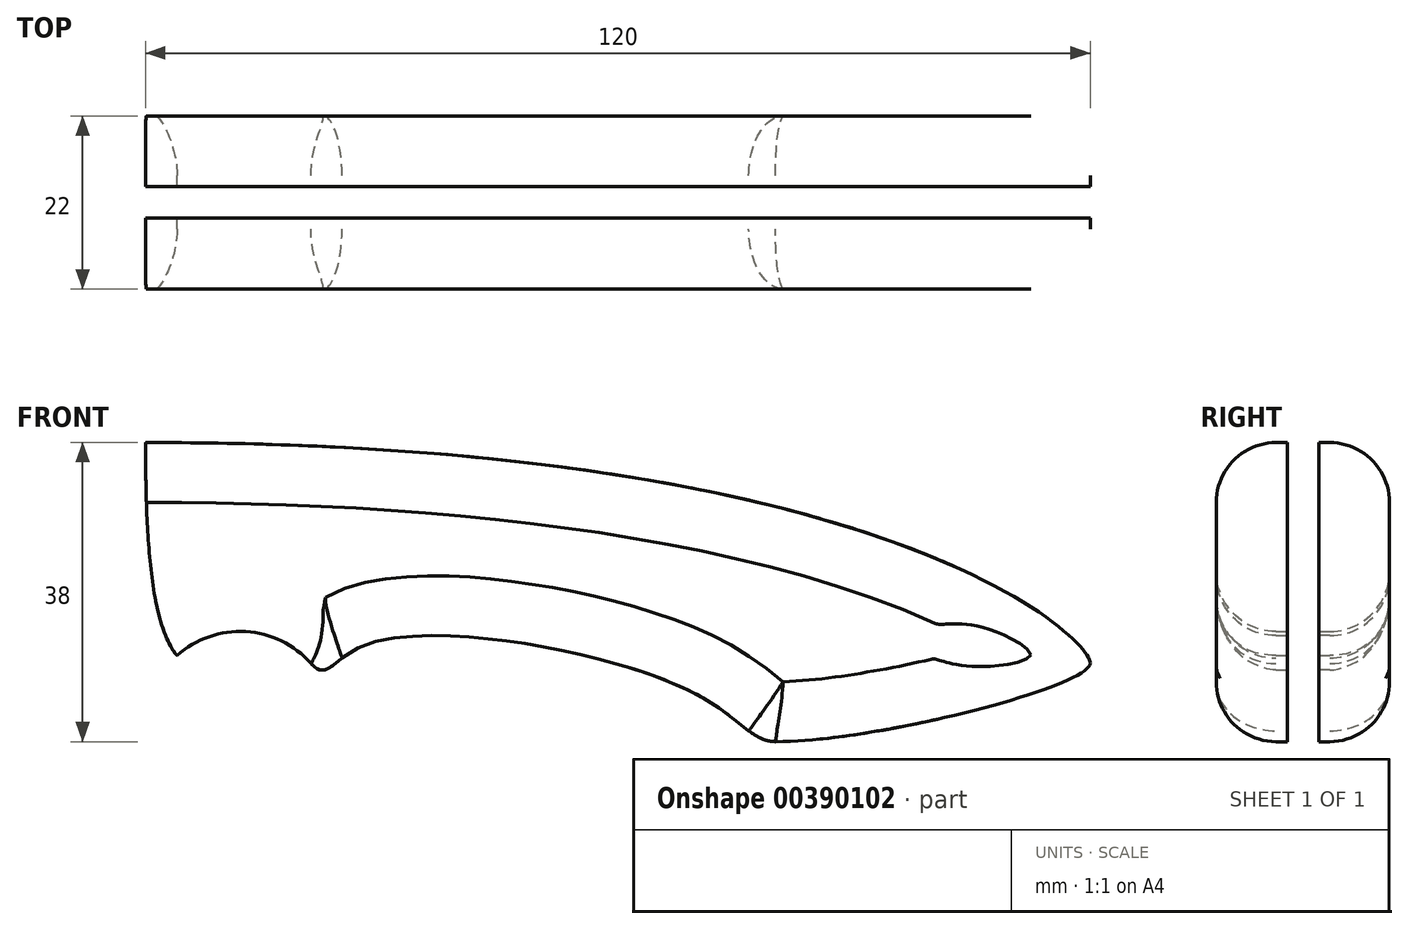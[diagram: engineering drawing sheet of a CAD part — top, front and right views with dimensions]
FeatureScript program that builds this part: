
annotation { "Feature Type Name" : "Feature", "Feature Type Description" : "" }
export const myFeature = defineFeature(function(context is Context, id is Id, definition is map)
    precondition{}
    {
        {
            var Q0;
            Q0=qCreatedBy(makeId("Front.planeOp"),FACE);
            var sketch = newSketch(context, id + "F0", { "sketchPlane" : qUnion([Q0])});
            skLineSegment(sketch, "E0.bottom", {"start": v(0, 0) * mm, "end": v(230, 0) * mm});
            skLineSegment(sketch, "E0.top", {"start": v(0, -38) * mm, "end": v(230, -38) * mm});
            skLineSegment(sketch, "E0.left", {"start": v(0, 0) * mm, "end": v(0, -38) * mm});
            skLineSegment(sketch, "E0.right", {"start": v(230, 0) * mm, "end": v(230, -38) * mm});
            skSolve(sketch);
        }
        {
            var Q0;
            Q0=makeQuery(id+"F0.imprint","IMPRINT",FACE,{"disambiguationData":[TD([[makeQuery(id+"F0.imprint","IMPRINT",EDGE,{"derivedFrom":sQuery(id+"F0.wireOp",EDGE,"E0.bottom")}),-1.0]])]});
            var sketch = newSketch(context, id + "F1", { "sketchPlane" : qUnion([Q0])});
            skLineSegment(sketch, "E1", {"start": v(0, 0) * mm, "end": v(0, -12) * mm});
            skLineSegment(sketch, "E2", {"start": v(110, 0) * mm, "end": v(230, 0) * mm});
            skFitSpline(sketch, "E3", {"points": [v(0, -12) * mm, v(110, 0) * mm], "startDerivative": vector(36.23, 12.3) * mm, "endDerivative": vector(240, 0) * mm});
            skFitSpline(sketch, "E4", {"points": [v(0, -12) * mm, v(110, -38) * mm], "startDerivative": vector(39.03, -50.57) * mm, "endDerivative": vector(165, 0) * mm});
            skFitSpline(sketch, "E5", {"points": [v(110, 0) * mm, v(230, -28) * mm], "startDerivative": vector(285, 0) * mm, "endDerivative": vector(0, -9) * mm});
            skLineSegment(sketch, "E6", {"start": v(110, -38) * mm, "end": v(110, -36) * mm});
            skLineSegment(sketch, "E7", {"start": v(110, -36) * mm, "end": v(122, -36) * mm, "construction": true});
            skArc(sketch, "E8", {"start": v(131, -28.06) * mm, "mid": v(117.76, -24.78) * mm, "end": v(110, -36) * mm});
            skLineSegment(sketch, "E9", {"start": v(131, -28.06) * mm, "end": v(132.98, -30.31) * mm});
            skFitSpline(sketch, "E10", {"points": [v(190, -38) * mm, v(180, -32) * mm, v(137, -26.06) * mm, v(131, -28.06) * mm], "startDerivative": vector(-33, 0) * mm, "endDerivative": vector(-29.63, 33.6) * mm});
            skFitSpline(sketch, "E11", {"points": [v(230, -28) * mm, v(190, -38) * mm], "startDerivative": vector(0, -9) * mm, "endDerivative": vector(-39, 0) * mm});
            skLineSegment(sketch, "E12", {"start": v(110, -28.06) * mm, "end": v(131, -28.06) * mm, "construction": true});
            skLineSegment(sketch, "E13", {"start": v(131, -26.06) * mm, "end": v(137, -26.06) * mm, "construction": true});
            skLineSegment(sketch, "E14", {"start": v(131, -28.06) * mm, "end": v(131, -26.06) * mm, "construction": true});
            skLineSegment(sketch, "E15", {"start": v(190, -38) * mm, "end": v(187, -38) * mm});
            skLineSegment(sketch, "E16", {"start": v(190, -32) * mm, "end": v(180, -32) * mm, "construction": true});
            skLineSegment(sketch, "E17", {"start": v(190, -38) * mm, "end": v(190, -32) * mm, "construction": true});
            skLineSegment(sketch, "E18", {"start": v(190, -38) * mm, "end": v(203, -38) * mm, "construction": true});
            skLineSegment(sketch, "E19", {"start": v(190, -38) * mm, "end": v(230, -38) * mm, "construction": true});
            skLineSegment(sketch, "E20", {"start": v(230, -28) * mm, "end": v(230, -25) * mm, "construction": true});
            skLineSegment(sketch, "E21", {"start": v(230, -28) * mm, "end": v(230, -31) * mm, "construction": true});
            skLineSegment(sketch, "E22", {"start": v(230, -28) * mm, "end": v(230, -38) * mm, "construction": true});
            skLineSegment(sketch, "E23", {"start": v(110, 0) * mm, "end": v(30, 0) * mm, "construction": true});
            skLineSegment(sketch, "E24", {"start": v(0, 0) * mm, "end": v(110, 0) * mm, "construction": true});
            skLineSegment(sketch, "E25", {"start": v(110, 0) * mm, "end": v(205, 0) * mm});
            skLineSegment(sketch, "E26", {"start": v(0, -12) * mm, "end": v(12.08, -7.9) * mm});
            skLineSegment(sketch, "E27", {"start": v(0, -12) * mm, "end": v(13.01, -28.86) * mm});
            skLineSegment(sketch, "E28", {"start": v(110, -27.06) * mm, "end": v(114, -27.06) * mm, "construction": true});
            skLineSegment(sketch, "E29", {"start": v(114, -27.06) * mm, "end": v(110, -22.58) * mm, "construction": true});
            skFitSpline(sketch, "E30", {"points": [v(110, 0) * mm, v(114, -27.06) * mm], "startDerivative": vector(0, -21) * mm, "endDerivative": vector(12, -13.42) * mm});
            skLineSegment(sketch, "E31", {"start": v(110, 0) * mm, "end": v(110, -7) * mm, "construction": true});
            skLineSegment(sketch, "E32", {"start": v(110, 0) * mm, "end": v(107, 0) * mm});
            skLineSegment(sketch, "E33", {"start": v(107, 0) * mm, "end": v(97, 0) * mm});
            skLineSegment(sketch, "E34", {"start": v(97, 0) * mm, "end": v(97, -14) * mm});
            skLineSegment(sketch, "E35", {"start": v(97, -14) * mm, "end": v(97, -24) * mm, "construction": true});
            skArc(sketch, "E36", {"start": v(107, -24) * mm, "mid": v(104.07, -16.92) * mm, "end": v(97, -14) * mm});
            skPoint(sketch, "E37", {"position": v(107, -24) * mm});
            skLineSegment(sketch, "E38", {"start": v(107, -24) * mm, "end": v(107, -38) * mm});
            skLineSegment(sketch, "E39", {"start": v(110, -38) * mm, "end": v(55, -38) * mm, "construction": true});
            skSolve(sketch);
        }
        {
            var Q0;
            {var subQ4=sQuery(id+"F1.wireOp",EDGE,"E3");Q0=makeQuery(id+"F1.imprint","IMPRINT",FACE,{"disambiguationData":[TD([[makeQuery(id+"F1.imprint","IMPRINT",EDGE,{"derivedFrom":subQ4}),-1.0]])]});}
            extrude(context, id + "F2", {"entities" : qUnion([Q0]), "endBound" : BoundingType.SYMMETRIC, "depth" : 4 * mm});
        }
        {
            var Q0;
            {var subQ5=sQuery(id+"F1.wireOp",EDGE,"E36");Q0=makeQuery(id+"F1.imprint","IMPRINT",FACE,{"disambiguationData":[TD([[makeQuery(id+"F1.imprint","IMPRINT",EDGE,{"derivedFrom":subQ5}),1.0]])]});}
            extrude(context, id + "F3", {"entities" : qUnion([Q0]), "operationType" : NewBodyOperationType.ADD, "endBound" : BoundingType.SYMMETRIC, "depth" : 4 * mm});
        }
        {
            var Q0;
            Q0=makeQuery(id+"F3.opExtrude","CAP_EDGE",EDGE,{"disambiguationData":[OSD([sQuery(id+"F1.wireOp",EDGE,"E4")])],"isStart":false});
            var Q1;
            Q1=makeQuery(id+"F3.opExtrude","CAP_EDGE",EDGE,{"disambiguationData":[OSD([sQuery(id+"F1.wireOp",EDGE,"E4")])],"isStart":true});
            chamfer(context, id + "F4", {"entities" : qUnion([Q0, Q1]), "chamferType" : ChamferType.TWO_OFFSETS, "width1" : 24 * mm, "oppositeDirection" : false, "width2" : 2 * mm, "tangentPropagation" : true});
        }
        {
            var Q0;
            {var subQ1=sQuery(id+"F1.wireOp",EDGE,"E6");Q0=makeQuery(id+"F1.imprint","IMPRINT",FACE,{"disambiguationData":[TD([[makeQuery(id+"F1.imprint","IMPRINT",EDGE,{"derivedFrom":subQ1}),1.0]])]});}
            var Q1;
            Q1=makeQuery(id+"F1.imprint","IMPRINT",FACE,{"disambiguationData":[TD([[makeQuery(id+"F1.imprint","IMPRINT",EDGE,{"derivedFrom":sQuery(id+"F1.wireOp",EDGE,"E5")}),-1.0]])]});
            extrude(context, id + "F5", {"entities" : qUnion([Q0, Q1]), "operationType" : NewBodyOperationType.ADD, "endBound" : BoundingType.SYMMETRIC, "depth" : 4 * mm});
        }
        {
            var Q0;
            Q0=makeQuery(id+"F1.imprint","IMPRINT",FACE,{"disambiguationData":[TD([[makeQuery(id+"F1.imprint","IMPRINT",EDGE,{"derivedFrom":sQuery(id+"F1.wireOp",EDGE,"E5")}),-1.0]])]});
            extrude(context, id + "F6", {"entities" : qUnion([Q0]), "endBound" : BoundingType.SYMMETRIC, "depth" : 22 * mm});
        }
        {
            var Q0;
            Q0=qSketchRegion(id+"F0",true);
            extrude(context, id + "F7", {"entities" : qUnion([Q0]), "operationType" : NewBodyOperationType.REMOVE, "endBound" : BoundingType.SYMMETRIC, "oppositeDirection" : true, "depth" : 4 * mm});
        }
        {
            var Q0;
            Q0=makeQuery(id+"F6.opExtrude","CAP_EDGE",EDGE,{"disambiguationData":[OSD([sQuery(id+"F1.wireOp",EDGE,"E5")])],"isStart":false});
            var Q1;
            Q1=makeQuery(id+"F6.opExtrude","CAP_EDGE",EDGE,{"disambiguationData":[OSD([sQuery(id+"F1.wireOp",EDGE,"E5")])],"isStart":true});
            fillet(context, id + "F8", {"entities" : qUnion([Q0, Q1]), "radius" : 7.6 * mm, "tangentPropagation" : true, "allowEdgeOverflow" : false});
        }
    });
